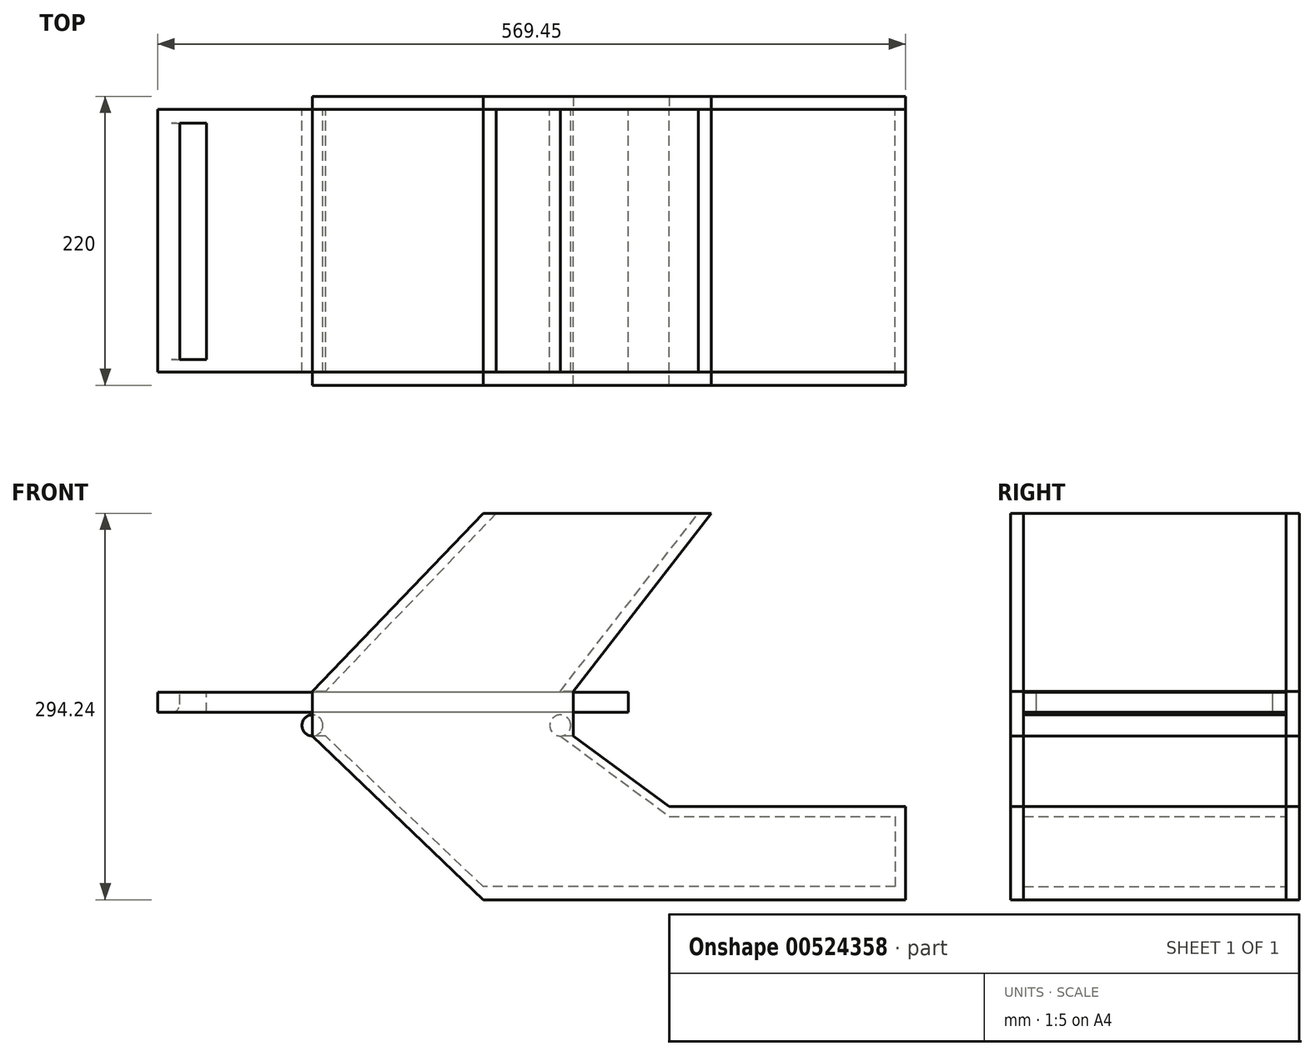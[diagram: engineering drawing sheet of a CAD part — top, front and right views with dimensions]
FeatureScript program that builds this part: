
annotation { "Feature Type Name" : "Feature", "Feature Type Description" : "" }
export const myFeature = defineFeature(function(context is Context, id is Id, definition is map)
    precondition{}
    {
        {
            var Q0;
            Q0=qCreatedBy(makeId("Front.planeOp"),FACE);
            var sketch = newSketch(context, id + "F0", { "sketchPlane" : qUnion([Q0])});
            skLineSegment(sketch, "E0", {"start": v(-88.74, 0) * mm, "end": v(41.26, 135.48) * mm});
            skLineSegment(sketch, "E1", {"start": v(41.26, 135.48) * mm, "end": v(51.26, 135.48) * mm});
            skLineSegment(sketch, "E2", {"start": v(51.26, 135.48) * mm, "end": v(-78.74, 0) * mm});
            skLineSegment(sketch, "E3", {"start": v(-78.74, 0) * mm, "end": v(-88.74, 0) * mm});
            skLineSegment(sketch, "E4", {"start": v(99.96, 0) * mm, "end": v(205.11, 135.48) * mm});
            skLineSegment(sketch, "E5", {"start": v(205.11, 135.48) * mm, "end": v(215.11, 135.48) * mm});
            skLineSegment(sketch, "E6", {"start": v(215.11, 135.48) * mm, "end": v(109.96, 0) * mm});
            skLineSegment(sketch, "E7", {"start": v(109.96, 0) * mm, "end": v(99.96, 0) * mm});
            skCircle(sketch, "E8", {"center": v(-88.74, -26.02) * mm, "radius": 8 * mm});
            skLineSegment(sketch, "E9", {"start": v(-88.74, -34.02) * mm, "end": v(41.26, -158.76) * mm});
            skLineSegment(sketch, "E10", {"start": v(41.26, -148.76) * mm, "end": v(-78.74, -34.02) * mm});
            skLineSegment(sketch, "E11", {"start": v(-78.74, -34.02) * mm, "end": v(-88.74, -34.02) * mm});
            skLineSegment(sketch, "E12", {"start": v(41.26, -158.76) * mm, "end": v(362.9, -158.76) * mm});
            skLineSegment(sketch, "E13", {"start": v(362.9, -158.76) * mm, "end": v(362.9, -87.9) * mm});
            skLineSegment(sketch, "E14", {"start": v(362.9, -87.9) * mm, "end": v(182.95, -87.9) * mm});
            skLineSegment(sketch, "E15", {"start": v(182.95, -87.9) * mm, "end": v(109.96, -34.02) * mm});
            skLineSegment(sketch, "E16", {"start": v(109.96, -34.02) * mm, "end": v(99.96, -34.02) * mm});
            skLineSegment(sketch, "E17", {"start": v(99.96, -34.02) * mm, "end": v(182.95, -95.29) * mm});
            skLineSegment(sketch, "E18", {"start": v(182.95, -95.29) * mm, "end": v(355.11, -95.29) * mm});
            skLineSegment(sketch, "E19", {"start": v(355.11, -95.29) * mm, "end": v(355.11, -148.76) * mm});
            skLineSegment(sketch, "E20", {"start": v(355.11, -148.76) * mm, "end": v(41.26, -148.76) * mm});
            skCircle(sketch, "E21", {"center": v(99.96, -26.02) * mm, "radius": 8 * mm});
            skLineSegment(sketch, "E22.bottom", {"start": v(126.82, -0.9) * mm, "end": v(-206.54, -0.9) * mm});
            skLineSegment(sketch, "E22.top", {"start": v(126.82, -16.16) * mm, "end": v(-206.54, -16.16) * mm});
            skLineSegment(sketch, "E22.left", {"start": v(126.82, -0.9) * mm, "end": v(126.82, -16.16) * mm});
            skLineSegment(sketch, "E22.right", {"start": v(-206.54, -0.9) * mm, "end": v(-206.54, -16.16) * mm});
            skSolve(sketch);
        }
        {
            var Q0;
            Q0 = qSketchRegion(id + "F0", true);
            extrude(context, id + "F1", {"entities" : qUnion([Q0]), "depth" : 200 * mm, "offsetDistance" : 25 * mm});
        }
        {
            var Q0;
            Q0=makeQuery(id+"F1.opExtrude","SWEPT_FACE",FACE,{"disambiguationData":[OSD([sQuery(id+"F0.wireOp",EDGE,"E22.bottom")])]});
            var sketch = newSketch(context, id + "F2", { "sketchPlane" : qUnion([Q0])});
            skLineSegment(sketch, "E23.bottom", {"start": v(-189.86, -10.29) * mm, "end": v(-169.44, -10.29) * mm});
            skLineSegment(sketch, "E23.top", {"start": v(-189.86, -190.29) * mm, "end": v(-169.44, -190.29) * mm});
            skLineSegment(sketch, "E23.left", {"start": v(-189.86, -10.29) * mm, "end": v(-189.86, -190.29) * mm});
            skLineSegment(sketch, "E23.right", {"start": v(-169.44, -10.29) * mm, "end": v(-169.44, -190.29) * mm});
            skSolve(sketch);
        }
        {
            var Q0;
            Q0 = qSketchRegion(id + "F2", true);
            extrude(context, id + "F3", {"entities" : qUnion([Q0]), "operationType" : NewBodyOperationType.REMOVE, "oppositeDirection" : true, "depth" : 25 * mm, "offsetDistance" : 25 * mm});
        }
        {
            var Q0;
            Q0=makeQuery(id+"F3.boolean.opBoolean","COPY",EDGE,{"derivedFrom":makeQuery(id+"F3.opExtrude","CAP_EDGE",EDGE,{"disambiguationData":[OSD([sQuery(id+"F2.wireOp",EDGE,"E23.left")])],"isStart":true})});
            var Q1;
            Q1=makeQuery(id+"F3.boolean.opBoolean","INTERSECT",EDGE,{"derivedFrom":[makeQuery(id+"F1.opExtrude","SWEPT_FACE",FACE,{"disambiguationData":[OSD([sQuery(id+"F0.wireOp",EDGE,"E22.top")])]}),makeQuery(id+"F3.opExtrude","SWEPT_FACE",FACE,{"disambiguationData":[OSD([sQuery(id+"F2.wireOp",EDGE,"E23.left")])]})]});
            fillet(context, id + "F4", {"entities" : qUnion([Q0, Q1]), "radius" : 6.28 * mm, "tangentPropagation" : true, "allowEdgeOverflow" : false});
        }
        {
            var Q0;
            Q0=makeQuery(id+"F1.opExtrude","CAP_VERTEX",VERTEX,{"disambiguationData":[OSD([sQuery(id+"F0.wireOp",EDGE,"E0"),sQuery(id+"F0.wireOp",EDGE,"E1")])],"isStart":false});
            var Q1;
            Q1=makeQuery(id+"F1.opExtrude","CAP_VERTEX",VERTEX,{"disambiguationData":[OSD([sQuery(id+"F0.wireOp",EDGE,"E9"),sQuery(id+"F0.wireOp",EDGE,"E12")])],"isStart":false});
            var Q2;
            Q2=makeQuery(id+"F1.opExtrude","CAP_VERTEX",VERTEX,{"disambiguationData":[OSD([sQuery(id+"F0.wireOp",EDGE,"E13"),sQuery(id+"F0.wireOp",EDGE,"E14")])],"isStart":false});
            cPlane(context, id + "F5", {"entities" : qUnion([Q0, Q1, Q2]), "cplaneType" : CPlaneType.THREE_POINT, "offset" : 25 * mm, "width" : 150 * mm, "height" : 150 * mm});
        }
        {
            var Q0;
            Q0=qCreatedBy(id+"F5.planeOp",FACE);
            var sketch = newSketch(context, id + "F6", { "sketchPlane" : qUnion([Q0])});
            skPoint(sketch, "E24", {"position": v(-41.26, 135.48) * mm});
            skPoint(sketch, "E25", {"position": v(-51.26, 135.48) * mm});
            skPoint(sketch, "E26", {"position": v(88.74, 0) * mm});
            skPoint(sketch, "E27", {"position": v(88.74, -34.02) * mm});
            skPoint(sketch, "E28", {"position": v(-41.26, -158.76) * mm});
            skPoint(sketch, "E29", {"position": v(-362.9, -158.76) * mm});
            skPoint(sketch, "E30", {"position": v(-362.9, -87.9) * mm});
            skPoint(sketch, "E31", {"position": v(-182.95, -87.9) * mm});
            skPoint(sketch, "E32", {"position": v(-109.96, -34.02) * mm});
            skPoint(sketch, "E33", {"position": v(-109.96, 0) * mm});
            skPoint(sketch, "E34", {"position": v(-215.11, 135.48) * mm});
            skPoint(sketch, "E35", {"position": v(-205.11, 135.48) * mm});
            skLineSegment(sketch, "E36", {"start": v(88.74, -34.02) * mm, "end": v(-41.26, -158.76) * mm});
            skLineSegment(sketch, "E37", {"start": v(-362.9, -158.76) * mm, "end": v(-362.9, -87.9) * mm});
            skLineSegment(sketch, "E38", {"start": v(-182.95, -87.9) * mm, "end": v(-109.96, -34.02) * mm});
            skLineSegment(sketch, "E39", {"start": v(-109.96, 0) * mm, "end": v(-215.11, 135.48) * mm});
            skLineSegment(sketch, "E40", {"start": v(-41.26, 135.48) * mm, "end": v(88.74, 0) * mm});
            skLineSegment(sketch, "E41", {"start": v(88.74, -34.02) * mm, "end": v(88.74, 0) * mm});
            skLineSegment(sketch, "E42", {"start": v(-109.96, -34.02) * mm, "end": v(-109.96, 0) * mm});
            skLineSegment(sketch, "E43", {"start": v(-215.11, 135.48) * mm, "end": v(-205.11, 135.48) * mm});
            skLineSegment(sketch, "E44", {"start": v(-205.11, 135.48) * mm, "end": v(-51.26, 135.48) * mm});
            skLineSegment(sketch, "E45", {"start": v(-51.26, 135.48) * mm, "end": v(-41.26, 135.48) * mm});
            skLineSegment(sketch, "E46", {"start": v(-182.95, -87.9) * mm, "end": v(-362.9, -87.9) * mm});
            skLineSegment(sketch, "E47", {"start": v(-362.9, -158.76) * mm, "end": v(-41.26, -158.76) * mm});
            skSolve(sketch);
        }
        {
            var Q0;
            Q0 = qSketchRegion(id + "F6", true);
            extrude(context, id + "F7", {"entities" : qUnion([Q0]), "oppositeDirection" : true, "depth" : 10 * mm, "offsetDistance" : 25 * mm});
        }
        {
            var Q0;
            Q0=makeQuery(id+"F1.opExtrude","SWEPT_FACE",FACE,{"disambiguationData":[OSD([sQuery(id+"F0.wireOp",EDGE,"E22.left")])]});
            extrude(context, id + "F8", {"entities" : qUnion([Q0]), "operationType" : NewBodyOperationType.ADD, "depth" : 25 * mm, "offsetDistance" : 25 * mm});
        }
        {
            var Q0;
            Q0=makeQuery(id+"F1.opExtrude","CAP_VERTEX",VERTEX,{"disambiguationData":[OSD([sQuery(id+"F0.wireOp",EDGE,"E12"),sQuery(id+"F0.wireOp",EDGE,"E13")])],"isStart":true});
            var Q1;
            Q1=makeQuery(id+"F1.opExtrude","CAP_VERTEX",VERTEX,{"disambiguationData":[OSD([sQuery(id+"F0.wireOp",EDGE,"E8"),sQuery(id+"F0.wireOp",EDGE,"E9"),sQuery(id+"F0.wireOp",EDGE,"E11")])],"isStart":true});
            var Q2;
            Q2=makeQuery(id+"F1.opExtrude","CAP_VERTEX",VERTEX,{"disambiguationData":[OSD([sQuery(id+"F0.wireOp",EDGE,"E5"),sQuery(id+"F0.wireOp",EDGE,"E6")])],"isStart":true});
            cPlane(context, id + "F9", {"entities" : qUnion([Q0, Q1, Q2]), "cplaneType" : CPlaneType.THREE_POINT, "offset" : 25 * mm, "width" : 150 * mm, "height" : 150 * mm});
        }
        {
            var Q0;
            Q0=qCreatedBy(id+"F9.planeOp",FACE);
            var sketch = newSketch(context, id + "F10", { "sketchPlane" : qUnion([Q0])});
            skPoint(sketch, "E48", {"position": v(362.9, -158.76) * mm});
            skPoint(sketch, "E49", {"position": v(362.9, -87.9) * mm});
            skPoint(sketch, "E50", {"position": v(182.95, -87.9) * mm});
            skPoint(sketch, "E51", {"position": v(109.96, -34.02) * mm});
            skPoint(sketch, "E52", {"position": v(109.96, 0) * mm});
            skPoint(sketch, "E53", {"position": v(215.11, 135.48) * mm});
            skPoint(sketch, "E54", {"position": v(41.26, 135.48) * mm});
            skPoint(sketch, "E55", {"position": v(-88.74, 0) * mm});
            skPoint(sketch, "E56", {"position": v(-88.74, -34.02) * mm});
            skPoint(sketch, "E57", {"position": v(41.26, -158.76) * mm});
            skLineSegment(sketch, "E58", {"start": v(362.9, -87.9) * mm, "end": v(362.9, -158.76) * mm});
            skLineSegment(sketch, "E59", {"start": v(41.26, -158.76) * mm, "end": v(-88.74, -34.02) * mm});
            skLineSegment(sketch, "E60", {"start": v(362.9, -158.76) * mm, "end": v(41.26, -158.76) * mm});
            skLineSegment(sketch, "E61", {"start": v(-88.74, -34.02) * mm, "end": v(-88.74, 0) * mm});
            skLineSegment(sketch, "E62", {"start": v(-88.74, 0) * mm, "end": v(41.26, 135.48) * mm});
            skLineSegment(sketch, "E63", {"start": v(41.26, 135.48) * mm, "end": v(215.11, 135.48) * mm});
            skLineSegment(sketch, "E64", {"start": v(215.11, 135.48) * mm, "end": v(109.96, 0) * mm});
            skLineSegment(sketch, "E65", {"start": v(109.96, 0) * mm, "end": v(109.96, -34.02) * mm});
            skLineSegment(sketch, "E66", {"start": v(109.96, -34.02) * mm, "end": v(182.95, -87.9) * mm});
            skLineSegment(sketch, "E67", {"start": v(182.95, -87.9) * mm, "end": v(362.9, -87.9) * mm});
            skSolve(sketch);
        }
        {
            var Q0;
            Q0 = qSketchRegion(id + "F10", true);
            extrude(context, id + "F11", {"entities" : qUnion([Q0]), "oppositeDirection" : true, "depth" : 10 * mm, "offsetDistance" : 25 * mm});
        }
    });
